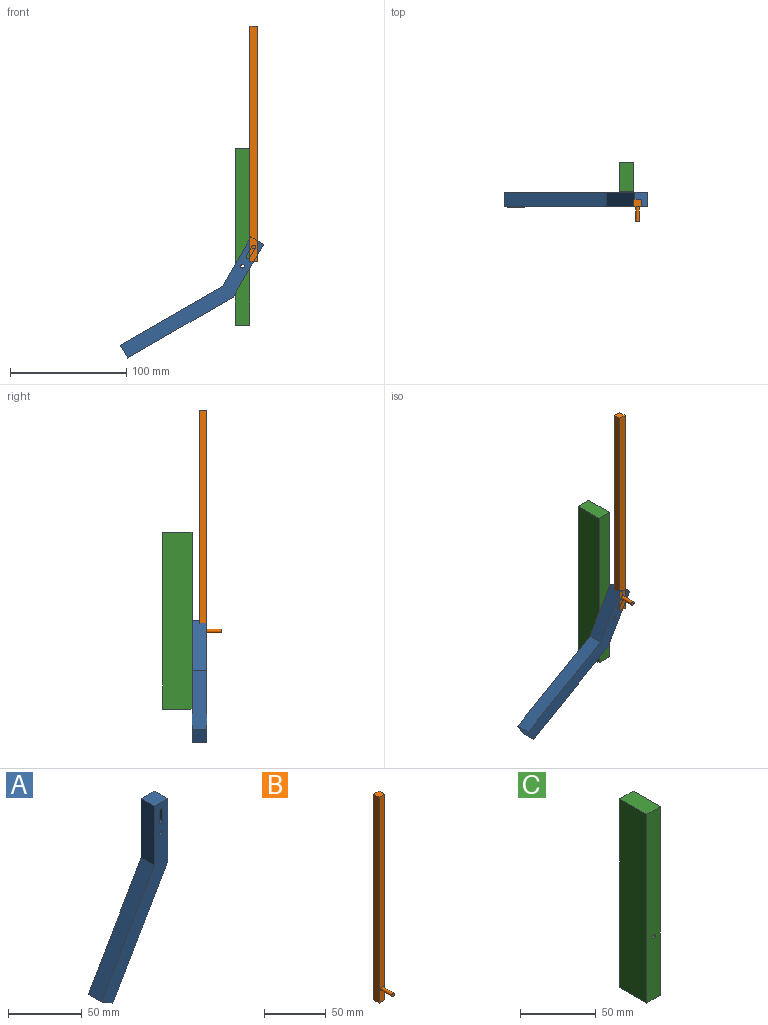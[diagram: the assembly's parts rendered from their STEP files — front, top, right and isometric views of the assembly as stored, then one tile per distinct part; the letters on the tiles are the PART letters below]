
ASSEMBLY  parts=3 mates=4
PART A: 13 faces, bbox 63.5x12.7x143.4 mm
  f0: plane 12.7x11mm, normal (-0.5,0,-0.87), area 161.3mm2, adj f1,f5,f6,f7
  f1: plane 90.94x52.5mm, normal (0.87,0,-0.5), area 1333.5mm2, adj f0,f2,f6,f7
  f2: plane 52.5x12.7mm, normal (1,0,0), area 666.8mm2, adj f1,f3,f6,f7
  f3: plane 12.7x12.7mm, normal (0,0,1), area 161.3mm2, adj f2,f4,f6,f7
  f4: plane 49.1x12.7mm, normal (-1,0,0), area 623.6mm2, adj f3,f5,f6,f7
  f5: plane 87.99x50.8mm, normal (-0.87,0,0.5), area 1290.3mm2, adj f0,f4,f6,f7
  f6: plane 143.44x63.5mm, normal (0,-1,0), area 1911mm2, adj f0,f1,f2,f3,f4,f5,f8,f9
  f7: plane 143.44x63.5mm, normal (0,1,0), area 1911mm2, adj f0,f1,f2,f3,f4,f5,f8,f9
  f8: cylinder r=1.59mm len=12.7mm, axis (0,-1,0), area 126.7mm2, adj f6,f7
  f9: plane 12.7x9.53mm, normal (-1,0,0), area 121mm2, adj f6,f7,f10,f12
  f10: cylinder r=1.59mm len=12.7mm, axis (0,-1,0), area 63.3mm2, adj f6,f7,f9,f11
  f11: plane 12.7x9.53mm, normal (1,0,0), area 121mm2, adj f6,f7,f10,f12
  f12: cylinder r=1.59mm len=12.7mm, axis (0,-1,0), area 63.3mm2, adj f6,f7,f9,f11
PART B: 8 faces, bbox 6.4x19.1x203.2 mm
  f0: plane 203.2x6.35mm, normal (1,0,0), area 1290.3mm2, adj f1,f3,f4,f5
  f1: plane 6.35x6.35mm, normal (0,0,1), area 40.3mm2, adj f0,f2,f4,f5
  f2: plane 203.2x6.35mm, normal (-1,0,0), area 1290.3mm2, adj f1,f3,f4,f5
  f3: plane 6.35x6.35mm, normal (0,0,-1), area 40.3mm2, adj f0,f2,f4,f5
  f4: plane 203.2x6.35mm, normal (0,-1,0), area 1282.4mm2, adj f0,f1,f2,f3,f6
  f5: plane 203.2x6.35mm, normal (0,1,0), area 1290.3mm2, adj f0,f1,f2,f3
  f6: cylinder r=1.59mm len=12.7mm, axis (0,1,0), area 126.7mm2, adj f4,f7
  f7: plane 3.18x3.18mm, normal (0,-1,0), area 7.9mm2, adj f6
PART C: 7 faces, bbox 12.7x25.4x152.4 mm
  f0: plane 25.4x12.7mm, normal (0,0,-1), area 322.6mm2, adj f1,f3,f4,f5
  f1: plane 152.4x25.4mm, normal (1,0,0), area 3871mm2, adj f0,f2,f4,f5
  f2: plane 25.4x12.7mm, normal (0,0,1), area 322.6mm2, adj f1,f3,f4,f5
  f3: plane 152.4x25.4mm, normal (-1,0,0), area 3871mm2, adj f0,f2,f4,f5
  f4: plane 152.4x12.7mm, normal (0,-1,0), area 1927.6mm2, adj f0,f1,f2,f3,f6
  f5: plane 152.4x12.7mm, normal (0,1,0), area 1927.6mm2, adj f0,f1,f2,f3,f6
  f6: cylinder r=1.59mm len=25.4mm, axis (0,-1,0), area 253.4mm2, adj f4,f5
PLACE A rot(axis=(0,1,0),30deg) t=(-50.63,-16.71,5.38)mm
PLACE B rot(axis=(1,0,0),0deg) t=(-27.55,-23.06,146.94)mm
PLACE C t=(-30.73,8.69,-9.25)mm fixed
MATE parallel B.f2 <-> C.f1  axis (-1,0,0) through (-30.73,-29.41,146.94)mm
MATE cylindrical B.f6 <-> A.f10  axis (0,1,0) through (-27.55,-35.76,58.04)mm
MATE pin_slot A.f10 <-> B.f6  axis (0,-1,0) through (-27.55,-29.41,58.04)mm
MATE revolute A.f8 <-> C.f6  axis (0,1,0) through (-37.08,-16.71,41.55)mm
